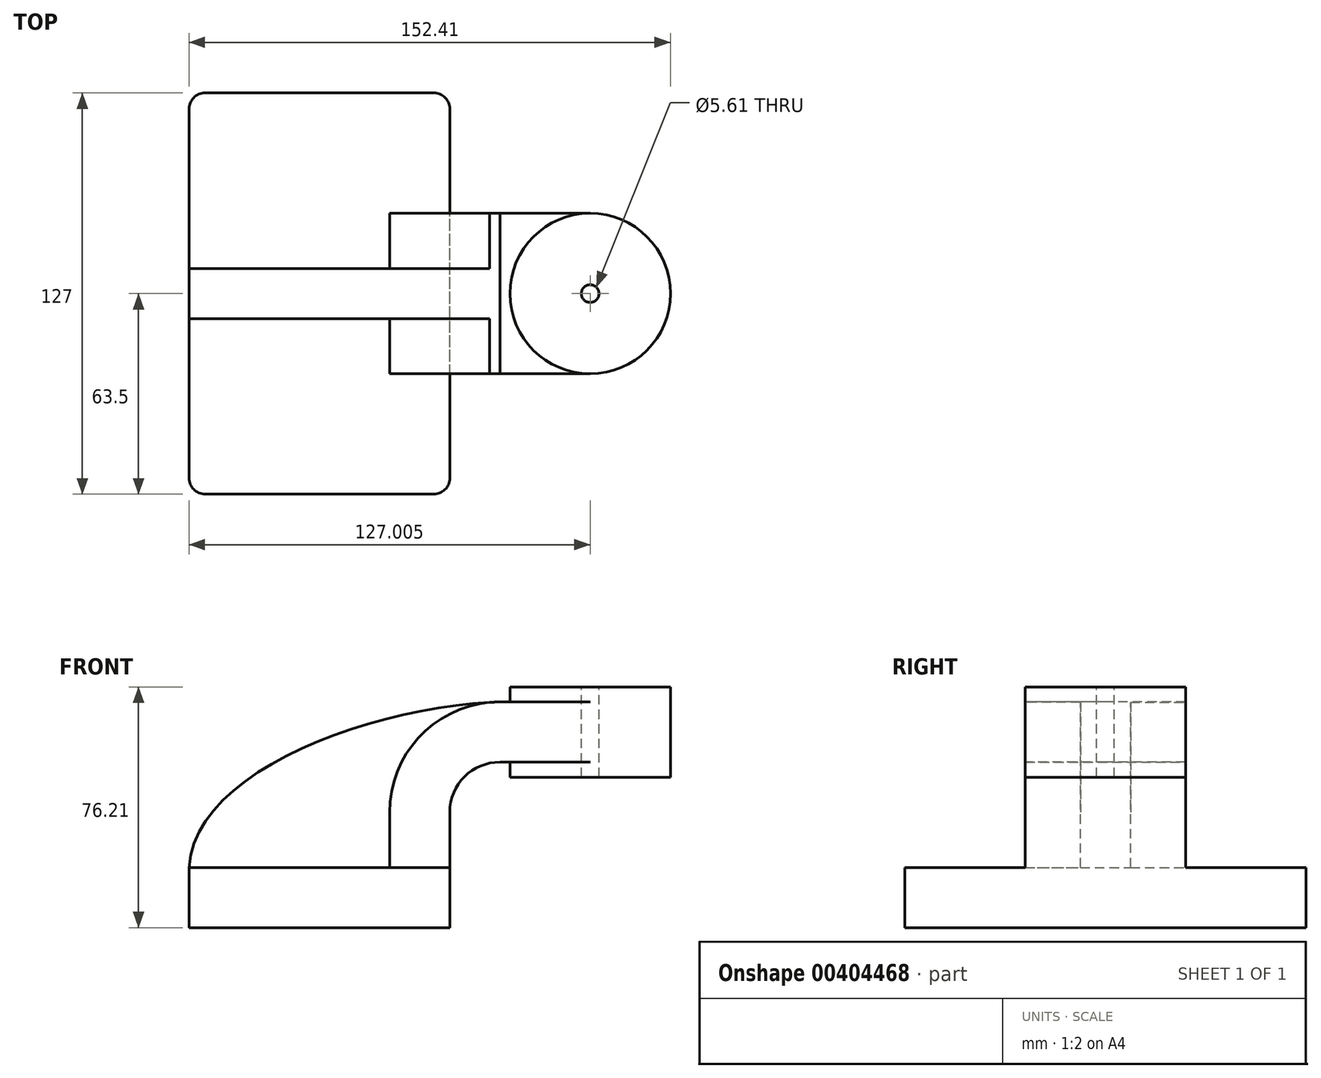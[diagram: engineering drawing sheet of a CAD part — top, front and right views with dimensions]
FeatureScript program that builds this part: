
annotation { "Feature Type Name" : "Feature", "Feature Type Description" : "" }
export const myFeature = defineFeature(function(context is Context, id is Id, definition is map)
    precondition{}
    {
        {
            var Q0;
            Q0=qCreatedBy(makeId("Front.planeOp"),FACE);
            var sketch = newSketch(context, id + "F0", { "sketchPlane" : qUnion([Q0])});
            skLineSegment(sketch, "E0.rect.bottom", {"start": v(-41.28, 9.52) * mm, "end": v(41.28, 9.52) * mm});
            skLineSegment(sketch, "E0.rect.top", {"start": v(-41.28, -9.52) * mm, "end": v(41.28, -9.52) * mm});
            skLineSegment(sketch, "E0.rect.left", {"start": v(-41.28, 9.52) * mm, "end": v(-41.28, -9.52) * mm});
            skLineSegment(sketch, "E0.rect.right", {"start": v(41.28, 9.52) * mm, "end": v(41.28, -9.52) * mm});
            skPoint(sketch, "E0.rect.middle", {"position": v(0, 0) * mm});
            skLineSegment(sketch, "E1", {"start": v(41.28, 9.52) * mm, "end": v(41.28, 27) * mm});
            skArc(sketch, "E2", {"start": v(41.28, 27) * mm, "mid": v(45.92, 38.23) * mm, "end": v(57.15, 42.88) * mm});
            skLineSegment(sketch, "E3", {"start": v(57.15, 42.88) * mm, "end": v(85.72, 42.88) * mm});
            skLineSegment(sketch, "E4.rect.bottom", {"start": v(60.32, 38.1) * mm, "end": v(111.12, 38.1) * mm});
            skLineSegment(sketch, "E4.rect.top", {"start": v(60.32, 66.68) * mm, "end": v(111.12, 66.68) * mm});
            skLineSegment(sketch, "E4.rect.left", {"start": v(60.32, 38.1) * mm, "end": v(60.32, 66.68) * mm});
            skLineSegment(sketch, "E4.rect.right", {"start": v(111.13, 38.1) * mm, "end": v(111.12, 66.68) * mm});
            skPoint(sketch, "E4.rect.middle", {"position": v(85.72, 52.39) * mm});
            skLineSegment(sketch, "E5.0", {"start": v(57.15, 61.93) * mm, "end": v(85.72, 61.93) * mm});
            skArc(sketch, "E5.1", {"start": v(22.23, 27) * mm, "mid": v(32.45, 51.7) * mm, "end": v(57.15, 61.93) * mm});
            skLineSegment(sketch, "E5.2", {"start": v(22.23, 9.52) * mm, "end": v(22.23, 27) * mm});
            skLineSegment(sketch, "E6", {"start": v(85.72, 38.1) * mm, "end": v(85.72, 66.68) * mm});
            skFitSpline(sketch, "E7", {"points": [v(-41.28, 9.53) * mm, v(57.15, 61.93) * mm], "startDerivative": vector(5.2, 92.34) * mm, "endDerivative": vector(120.92, 4.22) * mm});
            skSolve(sketch);
        }
        {
            var Q0;
            Q0=makeQuery(id+"F0.imprint","IMPRINT",FACE,{"disambiguationData":[TD([[makeQuery(id+"F0.imprint","IMPRINT",EDGE,{"derivedFrom":sQuery(id+"F0.wireOp",EDGE,"E0.rect.top")}),1.0]])]});
            extrude(context, id + "F1", {"entities" : qUnion([Q0]), "depth" : 127 * mm, "symmetric" : true});
        }
        {
            var Q0;
            {var subQ9=sQuery(id+"F0.wireOp",EDGE,"E1");Q0=makeQuery(id+"F0.imprint","IMPRINT",FACE,{"disambiguationData":[TD([[makeQuery(id+"F0.imprint","IMPRINT",EDGE,{"derivedFrom":subQ9}),1.0]])]});}
            var Q1;
            {var subQ0=sQuery(id+"F0.wireOp",EDGE,"E6");var subQ1=sQuery(id+"F0.wireOp",EDGE,"E3");var subQ2=makeQuery(id+"F0.imprint","INTERSECT",VERTEX,{"derivedFrom":[subQ1,subQ0]});Q1=makeQuery(id+"F0.imprint","IMPRINT",FACE,{"disambiguationData":[TD([[makeQuery(id+"F0.imprint","IMPRINT",EDGE,{"disambiguationData":[TD([[subQ2,1.0]])],"derivedFrom":subQ1}),1.0]])]});}
            extrude(context, id + "F2", {"entities" : qUnion([Q0, Q1]), "operationType" : NewBodyOperationType.ADD, "depth" : 50.8 * mm, "symmetric" : true});
        }
        {
            var Q0;
            {var subQ3=sQuery(id+"F0.wireOp",EDGE,"E5.2");Q0=makeQuery(id+"F0.imprint","IMPRINT",FACE,{"disambiguationData":[TD([[makeQuery(id+"F0.imprint","IMPRINT",EDGE,{"derivedFrom":subQ3}),1.0]])]});}
            extrude(context, id + "F3", {"entities" : qUnion([Q0]), "operationType" : NewBodyOperationType.ADD, "depth" : 15.88 * mm, "symmetric" : true});
        }
        {
            var Q0;
            {var subQ5=sQuery(id+"F0.wireOp",EDGE,"E4.rect.right");Q0=makeQuery(id+"F0.imprint","IMPRINT",FACE,{"disambiguationData":[TD([[makeQuery(id+"F0.imprint","IMPRINT",EDGE,{"derivedFrom":subQ5}),1.0]])]});}
            var Q1;
            Q1=sQuery(id+"F0.wireOp",EDGE,"E6");
            revolve(context, id + "F4", {"operationType" : NewBodyOperationType.ADD, "entities" : qUnion([Q0]), "axis" : qUnion([Q1]), "revolveType" : RevolveType.FULL});
        }
        {
            var Q0;
            Q0=makeQuery(id+"F1.opExtrude","CAP_EDGE",EDGE,{"disambiguationData":[OSD([sQuery(id+"F0.wireOp",EDGE,"E0.rect.right")])],"isStart":false});
            var Q1;
            Q1=makeQuery(id+"F1.opExtrude","CAP_EDGE",EDGE,{"disambiguationData":[OSD([sQuery(id+"F0.wireOp",EDGE,"E0.rect.left")])],"isStart":false});
            var Q2;
            Q2=makeQuery(id+"F1.opExtrude","CAP_EDGE",EDGE,{"disambiguationData":[OSD([sQuery(id+"F0.wireOp",EDGE,"E0.rect.right")])],"isStart":true});
            var Q3;
            Q3=makeQuery(id+"F1.opExtrude","CAP_EDGE",EDGE,{"disambiguationData":[OSD([sQuery(id+"F0.wireOp",EDGE,"E0.rect.left")])],"isStart":true});
            fillet(context, id + "F5", {"entities" : qUnion([Q0, Q1, Q2, Q3]), "radius" : 5.08 * mm, "tangentPropagation" : true, "allowEdgeOverflow" : false});
        }
        {
            var Q0;
            Q0=makeQuery(id+"F4.opRevolve","SWEPT_FACE",FACE,{"disambiguationData":[OSD([sQuery(id+"F0.wireOp",EDGE,"E4.rect.top")])]});
            var sketch = newSketch(context, id + "F6", { "sketchPlane" : qUnion([Q0])});
            skCircle(sketch, "E8", {"center": v(85.72, 0) * mm, "radius": 4.3 * mm});
            skSolve(sketch);
        }
        {
            var Q0;
            Q0=sQuery(id+"F6.wireOp",VERTEX,"E8.center");
            var Q1;
            Q1=makeQuery(id+"F1.opExtrude","SWEPT_BODY",BODY,{"disambiguationData":[OSD([sQuery(id+"F0.wireOp",EDGE,"E0.rect.bottom"),sQuery(id+"F0.wireOp",EDGE,"E0.rect.top"),sQuery(id+"F0.wireOp",EDGE,"E0.rect.left"),sQuery(id+"F0.wireOp",EDGE,"E0.rect.right")])]});
            hole(context, id + "F7", {"style" : HoleStyle.C_SINK, "endStyle" : HoleEndStyle.THROUGH, "holeDiameter" : 5.61 * mm, "cSinkDiameter" : 5.61 * mm, "cSinkAngle" : 82 * degree, "isTappedThrough" : true, "tappedDepth" : 12.7 * mm, "tapClearance" : 3, "startFromSketch" : true, "locations" : qUnion([Q0]), "scope" : qUnion([Q1])});
        }
    });
